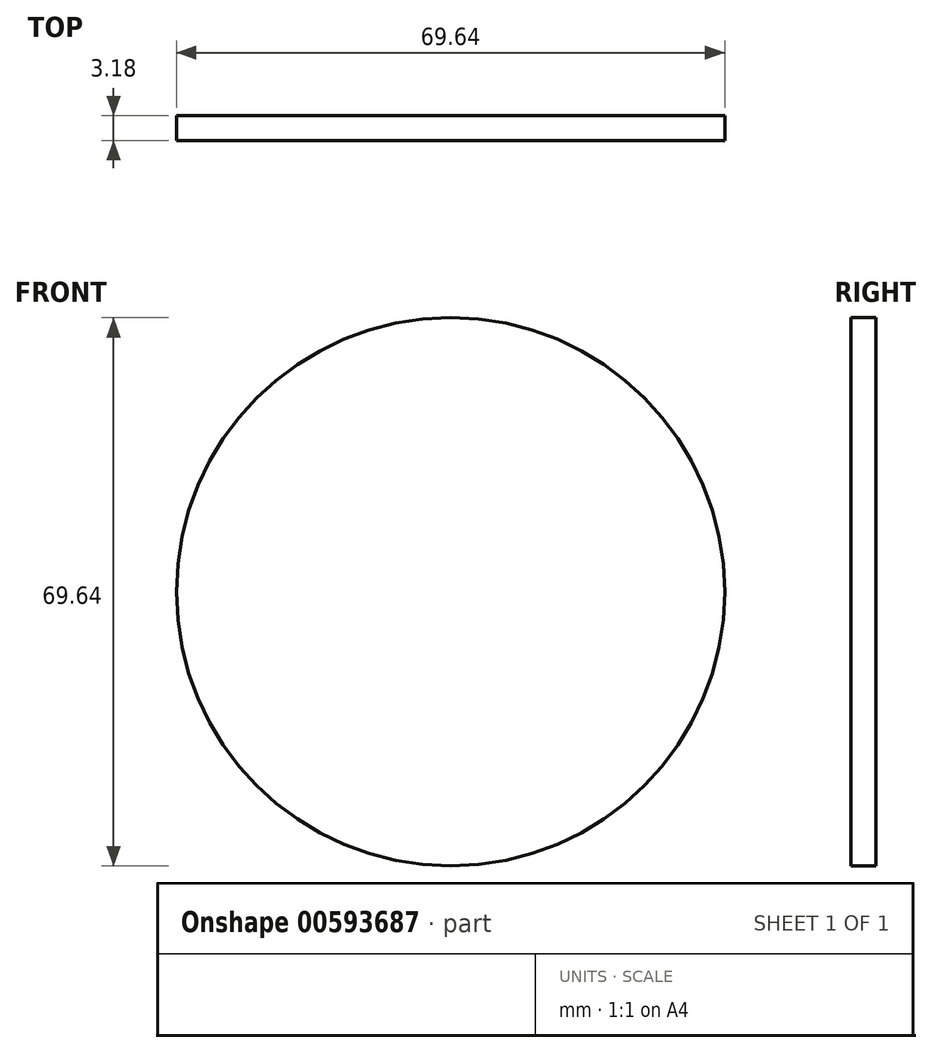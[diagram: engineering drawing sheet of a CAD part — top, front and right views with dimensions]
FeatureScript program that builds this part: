
annotation { "Feature Type Name" : "Feature", "Feature Type Description" : "" }
export const myFeature = defineFeature(function(context is Context, id is Id, definition is map)
    precondition{}
    {
        {
            var Q0;
            Q0=qCreatedBy(makeId("Front.planeOp"),FACE);
            var sketch = newSketch(context, id + "F0", { "sketchPlane" : qUnion([Q0])});
            skCircle(sketch, "E0", {"center": v(0, 0) * mm, "radius": 34.82 * mm});
            skSolve(sketch);
        }
        {
            var Q0;
            Q0=makeQuery(id+"F0.imprint","IMPRINT",FACE,{"disambiguationData":[TD([[makeQuery(id+"F0.imprint","IMPRINT",EDGE,{"derivedFrom":sQuery(id+"F0.wireOp",EDGE,"E0")}),1.0]])]});
            extrude(context, id + "F1", {"entities" : qUnion([Q0]), "depth" : 3.17 * mm, "offsetDistance" : 25.4 * mm});
        }
    });
